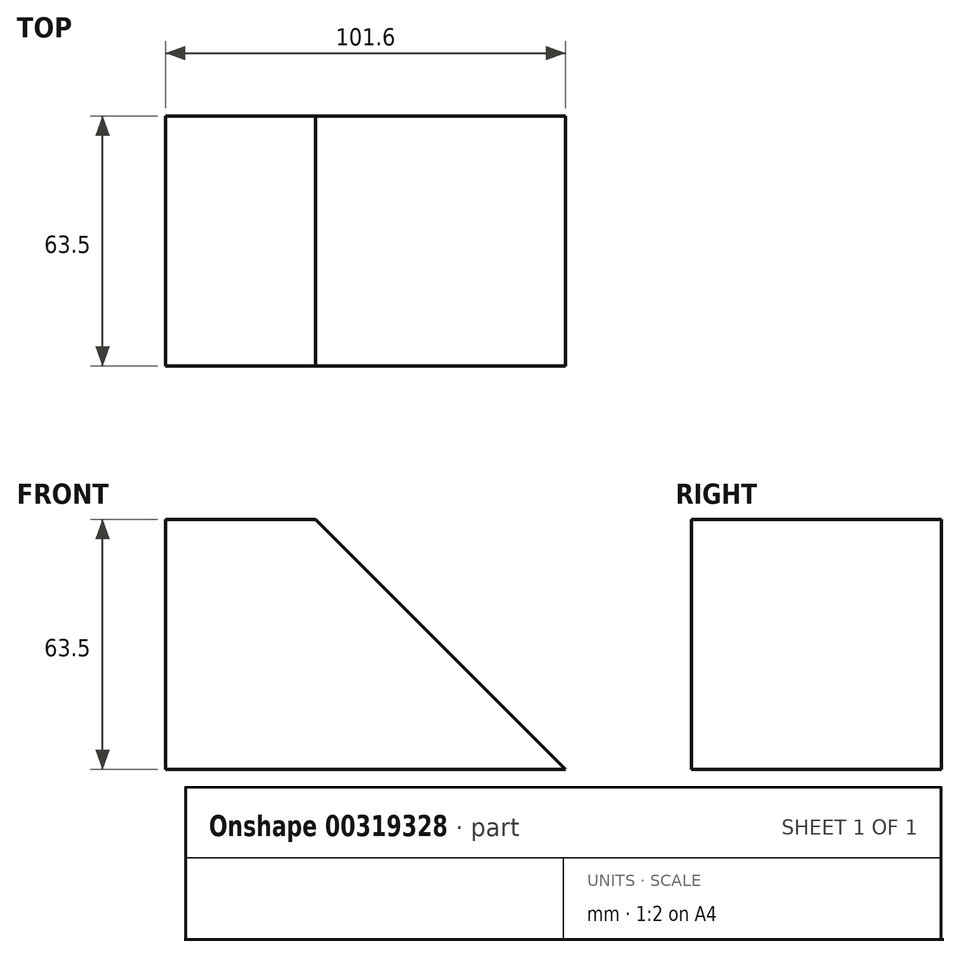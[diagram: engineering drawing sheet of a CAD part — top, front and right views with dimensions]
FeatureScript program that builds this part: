
annotation { "Feature Type Name" : "Feature", "Feature Type Description" : "" }
export const myFeature = defineFeature(function(context is Context, id is Id, definition is map)
    precondition{}
    {
        {
            var Q0;
            Q0=qCreatedBy(makeId("Front.planeOp"),FACE);
            var sketch = newSketch(context, id + "F0", { "sketchPlane" : qUnion([Q0])});
            skLineSegment(sketch, "E0", {"start": v(-48.73, -36.52) * mm, "end": v(52.87, -36.52) * mm});
            skLineSegment(sketch, "E1", {"start": v(52.87, -36.52) * mm, "end": v(-10.63, 26.98) * mm});
            skLineSegment(sketch, "E2", {"start": v(-10.63, 26.98) * mm, "end": v(-48.73, 26.98) * mm});
            skLineSegment(sketch, "E3", {"start": v(-48.73, 26.98) * mm, "end": v(-48.73, -36.52) * mm});
            skSolve(sketch);
        }
        {
            var Q0;
            Q0=makeQuery(id+"F0.imprint","IMPRINT",FACE,{"disambiguationData":[TD([[makeQuery(id+"F0.imprint","IMPRINT",EDGE,{"derivedFrom":sQuery(id+"F0.wireOp",EDGE,"E0")}),1.0]])]});
            extrude(context, id + "F1", {"entities" : qUnion([Q0]), "depth" : 63.5 * mm});
        }
    });
